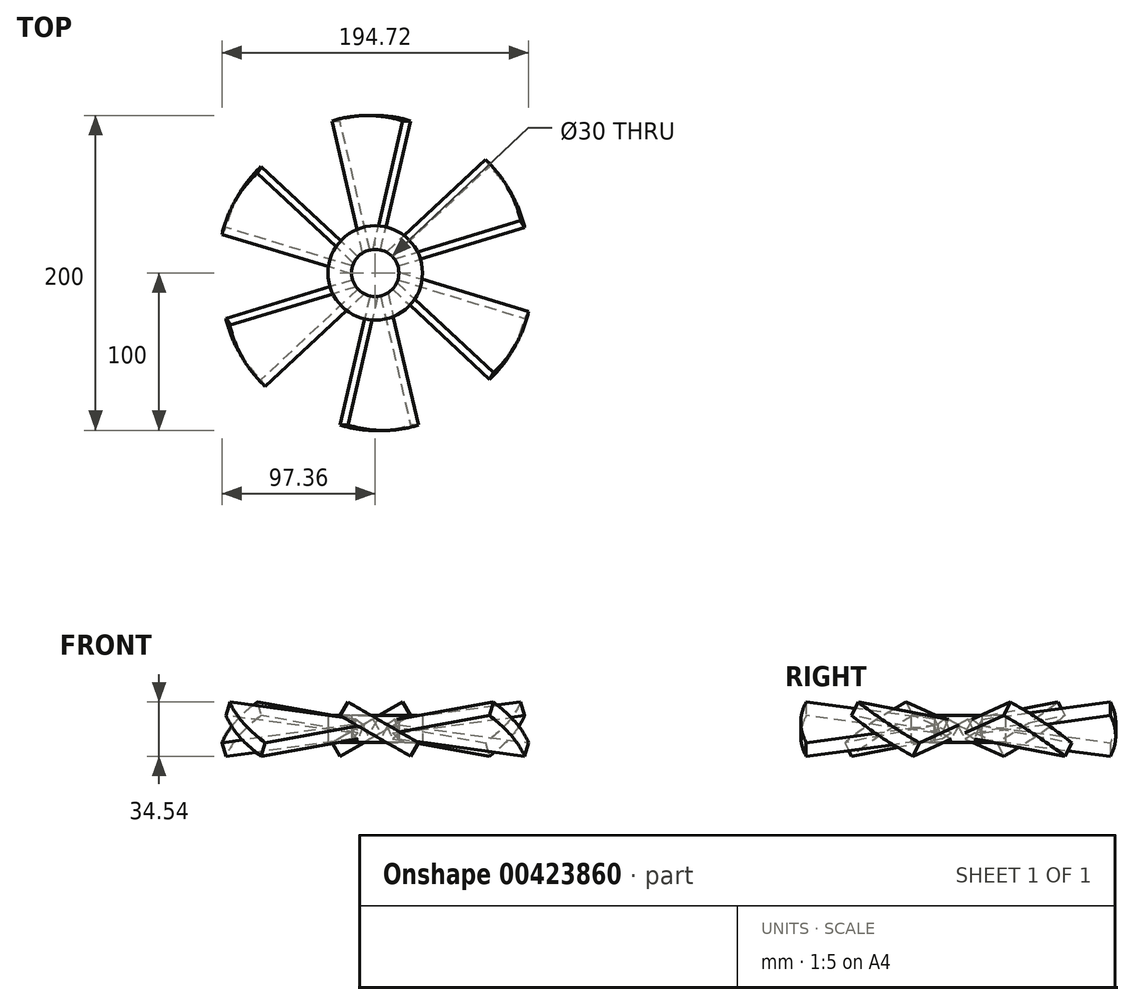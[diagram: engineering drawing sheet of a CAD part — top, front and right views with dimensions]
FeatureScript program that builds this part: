
annotation { "Feature Type Name" : "Feature", "Feature Type Description" : "" }
export const myFeature = defineFeature(function(context is Context, id is Id, definition is map)
    precondition{}
    {
        {
            var Q0;
            Q0=qCreatedBy(makeId("Top.planeOp"),FACE);
            var sketch = newSketch(context, id + "F0", { "sketchPlane" : qUnion([Q0])});
            skArc(sketch, "E0", {"start": v(25.88, 96.6) * mm, "mid": v(0, 100) * mm, "end": v(-25.88, 96.6) * mm});
            skLineSegment(sketch, "E1", {"start": v(0, 0) * mm, "end": v(-25.88, 96.6) * mm});
            skLineSegment(sketch, "E2", {"start": v(0, 0) * mm, "end": v(25.88, 96.6) * mm});
            skLineSegment(sketch, "E3", {"start": v(0, 0) * mm, "end": v(0, 120.55) * mm});
            skLineSegment(sketch, "E4", {"start": v(0, 120.55) * mm, "end": v(0, -26.3) * mm});
            skSolve(sketch);
        }
        {
            var Q0;
            Q0 = qSketchRegion(id + "F0", true);
            extrude(context, id + "F1", {"entities" : qUnion([Q0]), "depth" : 10 * mm});
        }
        {
            var Q0;
            Q0=qCreatedBy(makeId("Top.planeOp"),FACE);
            var sketch = newSketch(context, id + "F2", { "sketchPlane" : qUnion([Q0])});
            skLineSegment(sketch, "E5", {"start": v(0, 99.86) * mm, "end": v(0, -17.39) * mm});
            skSolve(sketch);
        }
        {
            var Q0;
            Q0=makeQuery(id+"F1.opExtrude","SWEPT_BODY",BODY,{"disambiguationData":[OSD([sQuery(id+"F0.wireOp",EDGE,"E0"),sQuery(id+"F0.wireOp",EDGE,"E1"),sQuery(id+"F0.wireOp",EDGE,"E2")])]});
            var Q1;
            Q1=sQuery(id+"F2.wireOp",EDGE,"E5");
            transform(context, id + "F3", {"entities" : qUnion([Q0]), "transformType" : TransformType.ROTATION, "transformAxis" : qUnion([Q1]), "angle" : 30 * degree, "makeCopy" : false});
        }
        {
            var Q0;
            Q0=qCreatedBy(makeId("Front.planeOp"),FACE);
            var sketch = newSketch(context, id + "F4", { "sketchPlane" : qUnion([Q0])});
            skLineSegment(sketch, "E6", {"start": v(0, 21.4) * mm, "end": v(0, -15.37) * mm});
            skSolve(sketch);
        }
        {
            var Q0;
            Q0=makeQuery(id+"F1.opExtrude","SWEPT_BODY",BODY,{"disambiguationData":[OSD([sQuery(id+"F0.wireOp",EDGE,"E0"),sQuery(id+"F0.wireOp",EDGE,"E1"),sQuery(id+"F0.wireOp",EDGE,"E2")])]});
            var Q1;
            Q1=sQuery(id+"F4.wireOp",EDGE,"E6");
            circularPattern(context, id + "F5", {"entities" : qUnion([Q0]), "axis" : qUnion([Q1]), "angle" : 360 * degree, "instanceCount" : 6, "equalSpace" : true});
        }
        {
            var Q0;
            Q0=qCreatedBy(makeId("Top.planeOp"),FACE);
            var sketch = newSketch(context, id + "F6", { "sketchPlane" : qUnion([Q0])});
            skCircle(sketch, "E7", {"center": v(0, 0) * mm, "radius": 30 * mm});
            skCircle(sketch, "E8", {"center": v(0, 0) * mm, "radius": 15 * mm});
            skSolve(sketch);
        }
        {
            var Q0;
            Q0 = qSketchRegion(id + "F6", true);
            extrude(context, id + "F7", {"entities" : qUnion([Q0]), "depth" : 13 * mm, "hasSecondDirection" : true, "secondDirectionOppositeDirection" : true, "secondDirectionDepth" : 4 * mm});
        }
        {
            var Q0;
            Q0=qCreatedBy(makeId("Top.planeOp"),FACE);
            var sketch = newSketch(context, id + "F8", { "sketchPlane" : qUnion([Q0])});
            skCircle(sketch, "E9", {"center": v(0, 0) * mm, "radius": 15 * mm});
            skSolve(sketch);
        }
        {
            var Q0;
            Q0 = qSketchRegion(id + "F8", true);
            extrude(context, id + "F9", {"entities" : qUnion([Q0]), "operationType" : NewBodyOperationType.REMOVE, "oppositeDirection" : true, "depth" : 25 * mm, "hasSecondDirection" : true, "secondDirectionOppositeDirection" : false, "secondDirectionDepth" : 25 * mm});
        }
    });
